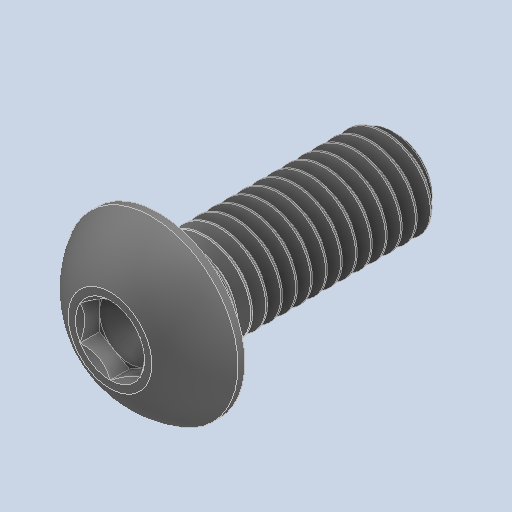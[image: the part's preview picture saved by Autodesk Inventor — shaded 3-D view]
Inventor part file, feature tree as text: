
AUTODESK INVENTOR PART (.ipt)
format: ipt  version: 2024.2 (Build 282272000, 272)  size: 549,888 bytes
history: native  units: in
note: dims shown in document units (in); Inventor stores cm internally (conversion verified against a paired STEP export)
features: revolve x1
ambient origin geometry x8: Origin, YZ Plane, XZ Plane, XY Plane, X Axis, Y Axis, Z Axis, Center Point
bodies: Solid1 (feature_tree)
feature tree (1):
  revolve  "Revolve2"  [1 undecoded]
note: 1 required parameter value undecoded (feature->parameter linkage not recoverable at this tier; creation-order binding heuristic only, values carry confidence <= 0.55)
